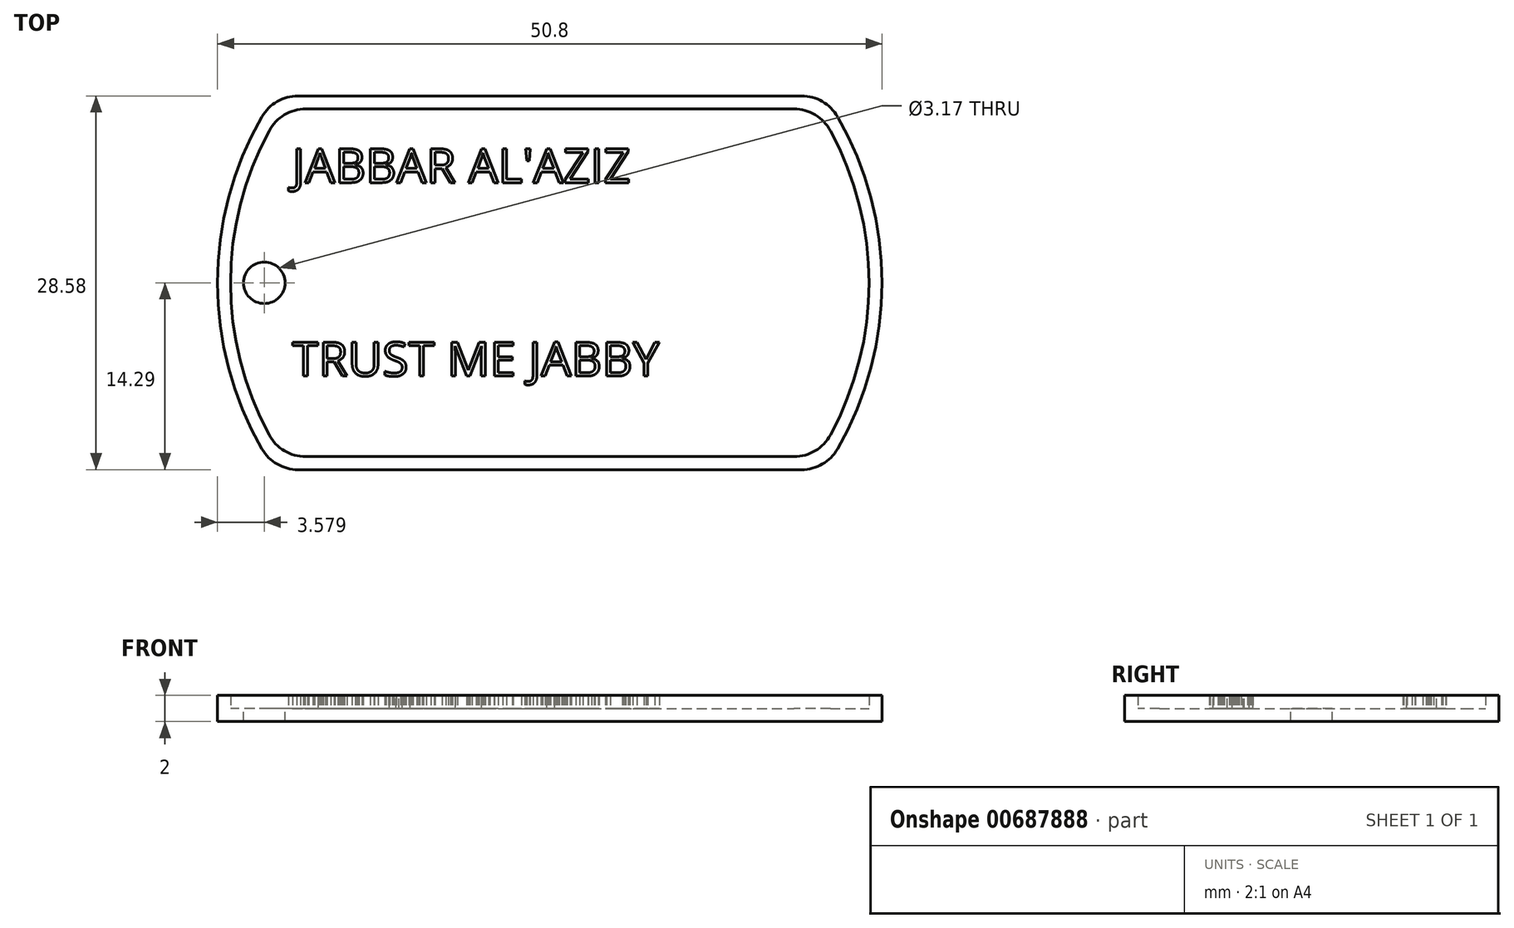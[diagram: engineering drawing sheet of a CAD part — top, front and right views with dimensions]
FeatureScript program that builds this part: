
annotation { "Feature Type Name" : "Feature", "Feature Type Description" : "" }
export const myFeature = defineFeature(function(context is Context, id is Id, definition is map)
    precondition{}
    {
        {
            var Q0;
            Q0=qCreatedBy(makeId("Top.planeOp"),FACE);
            var sketch = newSketch(context, id + "F0", { "sketchPlane" : qUnion([Q0])});
            skArc(sketch, "E0", {"start": v(-22, 12.7) * mm, "mid": v(-25.4, 0) * mm, "end": v(-22, -12.7) * mm});
            skLineSegment(sketch, "E1.top", {"start": v(-19.25, -14.29) * mm, "end": v(19.25, -14.29) * mm});
            skArc(sketch, "E2.trimOffspring", {"start": v(22, -12.7) * mm, "mid": v(25.4, 0) * mm, "end": v(22, 12.7) * mm});
            skLineSegment(sketch, "E3", {"start": v(-19.25, 14.29) * mm, "end": v(19.25, 14.29) * mm});
            skPoint(sketch, "E4.visualSharp", {"position": v(-21, 14.29) * mm});
            skArc(sketch, "E4.filletArc", {"start": v(-19.25, 14.29) * mm, "mid": v(-20.83, 13.86) * mm, "end": v(-22, 12.7) * mm});
            skPoint(sketch, "E5.visualSharp", {"position": v(21, 14.29) * mm});
            skArc(sketch, "E5.filletArc", {"start": v(22, 12.7) * mm, "mid": v(20.83, 13.86) * mm, "end": v(19.25, 14.29) * mm});
            skPoint(sketch, "E6.visualSharp", {"position": v(21, -14.29) * mm});
            skArc(sketch, "E6.filletArc", {"start": v(19.25, -14.29) * mm, "mid": v(20.83, -13.86) * mm, "end": v(22, -12.7) * mm});
            skPoint(sketch, "E7.visualSharp", {"position": v(-21, -14.29) * mm});
            skArc(sketch, "E7.filletArc", {"start": v(-22, -12.7) * mm, "mid": v(-20.83, -13.86) * mm, "end": v(-19.25, -14.29) * mm});
            skSolve(sketch);
        }
        {
            var Q0;
            Q0=makeQuery(id+"F0.imprint","IMPRINT",FACE,{"disambiguationData":[TD([[makeQuery(id+"F0.imprint","IMPRINT",EDGE,{"derivedFrom":sQuery(id+"F0.wireOp",EDGE,"E0")}),1.0]])]});
            extrude(context, id + "F1", {"entities" : qUnion([Q0]), "depth" : 1 * mm, "offsetDistance" : 25.4 * mm});
        }
        {
            var Q0;
            Q0=makeQuery(id+"F1.opExtrude","CAP_FACE",FACE,{"disambiguationData":[OSD([sQuery(id+"F0.wireOp",EDGE,"E0"),sQuery(id+"F0.wireOp",EDGE,"E1.top"),sQuery(id+"F0.wireOp",EDGE,"E2.trimOffspring"),sQuery(id+"F0.wireOp",EDGE,"E3"),sQuery(id+"F0.wireOp",EDGE,"E4.filletArc"),sQuery(id+"F0.wireOp",EDGE,"E5.filletArc"),sQuery(id+"F0.wireOp",EDGE,"E6.filletArc"),sQuery(id+"F0.wireOp",EDGE,"E7.filletArc")])],"isStart":false});
            var sketch = newSketch(context, id + "F2", { "sketchPlane" : qUnion([Q0])});
            skLineSegment(sketch, "E8.0", {"start": v(-18.66, 13.29) * mm, "end": v(18.66, 13.29) * mm});
            skArc(sketch, "E8.1", {"start": v(-21.45, 11.63) * mm, "mid": v(-24.4, 0) * mm, "end": v(-21.45, -11.63) * mm});
            skLineSegment(sketch, "E8.2", {"start": v(-18.66, -13.29) * mm, "end": v(18.66, -13.29) * mm});
            skArc(sketch, "E8.3", {"start": v(21.45, -11.63) * mm, "mid": v(24.4, 0) * mm, "end": v(21.45, 11.63) * mm});
            skPoint(sketch, "E9.visualSharp", {"position": v(-20.46, 13.29) * mm});
            skArc(sketch, "E9.filletArc", {"start": v(-18.66, 13.29) * mm, "mid": v(-20.29, 12.84) * mm, "end": v(-21.45, 11.63) * mm});
            skPoint(sketch, "E10.visualSharp", {"position": v(20.46, 13.29) * mm});
            skArc(sketch, "E10.filletArc", {"start": v(21.45, 11.63) * mm, "mid": v(20.29, 12.84) * mm, "end": v(18.66, 13.29) * mm});
            skPoint(sketch, "E11.visualSharp", {"position": v(20.46, -13.29) * mm});
            skArc(sketch, "E11.filletArc", {"start": v(18.66, -13.29) * mm, "mid": v(20.29, -12.84) * mm, "end": v(21.45, -11.63) * mm});
            skPoint(sketch, "E12.visualSharp", {"position": v(-20.46, -13.29) * mm});
            skArc(sketch, "E12.filletArc", {"start": v(-21.45, -11.63) * mm, "mid": v(-20.29, -12.84) * mm, "end": v(-18.66, -13.29) * mm});
            skLineSegment(sketch, "E13.0", {"start": v(-19.25, 14.29) * mm, "end": v(19.25, 14.29) * mm});
            skArc(sketch, "E13.1", {"start": v(-22, 12.7) * mm, "mid": v(-25.4, 0) * mm, "end": v(-22, -12.7) * mm});
            skLineSegment(sketch, "E13.2", {"start": v(-19.25, -14.29) * mm, "end": v(19.25, -14.29) * mm});
            skArc(sketch, "E13.3", {"start": v(22, -12.7) * mm, "mid": v(25.4, 0) * mm, "end": v(22, 12.7) * mm});
            skPoint(sketch, "E14.visualSharp", {"position": v(-21, -14.29) * mm});
            skArc(sketch, "E14.filletArc", {"start": v(-22, -12.7) * mm, "mid": v(-20.83, -13.86) * mm, "end": v(-19.25, -14.29) * mm});
            skPoint(sketch, "E15.visualSharp", {"position": v(21, -14.29) * mm});
            skArc(sketch, "E15.filletArc", {"start": v(19.25, -14.29) * mm, "mid": v(20.83, -13.86) * mm, "end": v(22, -12.7) * mm});
            skPoint(sketch, "E16.visualSharp", {"position": v(21, 14.29) * mm});
            skArc(sketch, "E16.filletArc", {"start": v(22, 12.7) * mm, "mid": v(20.83, 13.86) * mm, "end": v(19.25, 14.29) * mm});
            skPoint(sketch, "E17.visualSharp", {"position": v(-21, 14.29) * mm});
            skArc(sketch, "E17.filletArc", {"start": v(-19.25, 14.29) * mm, "mid": v(-20.83, 13.86) * mm, "end": v(-22, 12.7) * mm});
            skSolve(sketch);
        }
        {
            var Q0;
            Q0=makeQuery(id+"F2.imprint","IMPRINT",FACE,{"disambiguationData":[TD([[makeQuery(id+"F2.imprint","IMPRINT",EDGE,{"derivedFrom":sQuery(id+"F2.wireOp",EDGE,"E8.0")}),1.0]])]});
            extrude(context, id + "F3", {"entities" : qUnion([Q0]), "operationType" : NewBodyOperationType.ADD, "depth" : 1 * mm, "offsetDistance" : 25.4 * mm});
        }
        {
            var Q0;
            Q0=makeQuery(id+"F1.opExtrude","CAP_FACE",FACE,{"disambiguationData":[OSD([sQuery(id+"F0.wireOp",EDGE,"E0"),sQuery(id+"F0.wireOp",EDGE,"E1.top"),sQuery(id+"F0.wireOp",EDGE,"E2.trimOffspring"),sQuery(id+"F0.wireOp",EDGE,"E3"),sQuery(id+"F0.wireOp",EDGE,"E4.filletArc"),sQuery(id+"F0.wireOp",EDGE,"E5.filletArc"),sQuery(id+"F0.wireOp",EDGE,"E6.filletArc"),sQuery(id+"F0.wireOp",EDGE,"E7.filletArc")])],"isStart":false});
            var sketch = newSketch(context, id + "F4", { "sketchPlane" : qUnion([Q0])});
            skCircle(sketch, "E18", {"center": v(-21.82, 0) * mm, "radius": 1.59 * mm});
            skSolve(sketch);
        }
        {
            var Q0;
            Q0=makeQuery(id+"F4.imprint","IMPRINT",FACE,{"disambiguationData":[TD([[makeQuery(id+"F4.imprint","IMPRINT",EDGE,{"derivedFrom":sQuery(id+"F4.wireOp",EDGE,"E18")}),1.0]])]});
            extrude(context, id + "F5", {"entities" : qUnion([Q0]), "operationType" : NewBodyOperationType.REMOVE, "oppositeDirection" : true, "depth" : 1 * mm, "offsetDistance" : 25.4 * mm});
        }
        {
            var Q0;
            Q0=makeQuery(id+"F2.imprint","IMPRINT",FACE,{"disambiguationData":[TD([[makeQuery(id+"F2.imprint","IMPRINT",EDGE,{"derivedFrom":sQuery(id+"F2.wireOp",EDGE,"E8.0")}),-1.0]])]});
            var sketch = newSketch(context, id + "F6", { "sketchPlane" : qUnion([Q0])});
            skText(sketch, "E19", { "text": "JABBAR AL\'AZIZ\n\n\nTRUST ME JABBY", "fontName": "OpenSans-Regular.ttf"});
            const initialGuessF6  = {"E19": [-0.01968, 0.00766, 1, 0, 0.00261]};
            skSetInitialGuess(sketch, initialGuessF6);
            skSolve(sketch);
        }
        {
            var Q0;
            Q0 = qSketchRegion(id + "F6", true);
            extrude(context, id + "F7", {"entities" : qUnion([Q0]), "operationType" : NewBodyOperationType.ADD, "depth" : 1 * mm, "offsetDistance" : 25.4 * mm});
        }
    });
